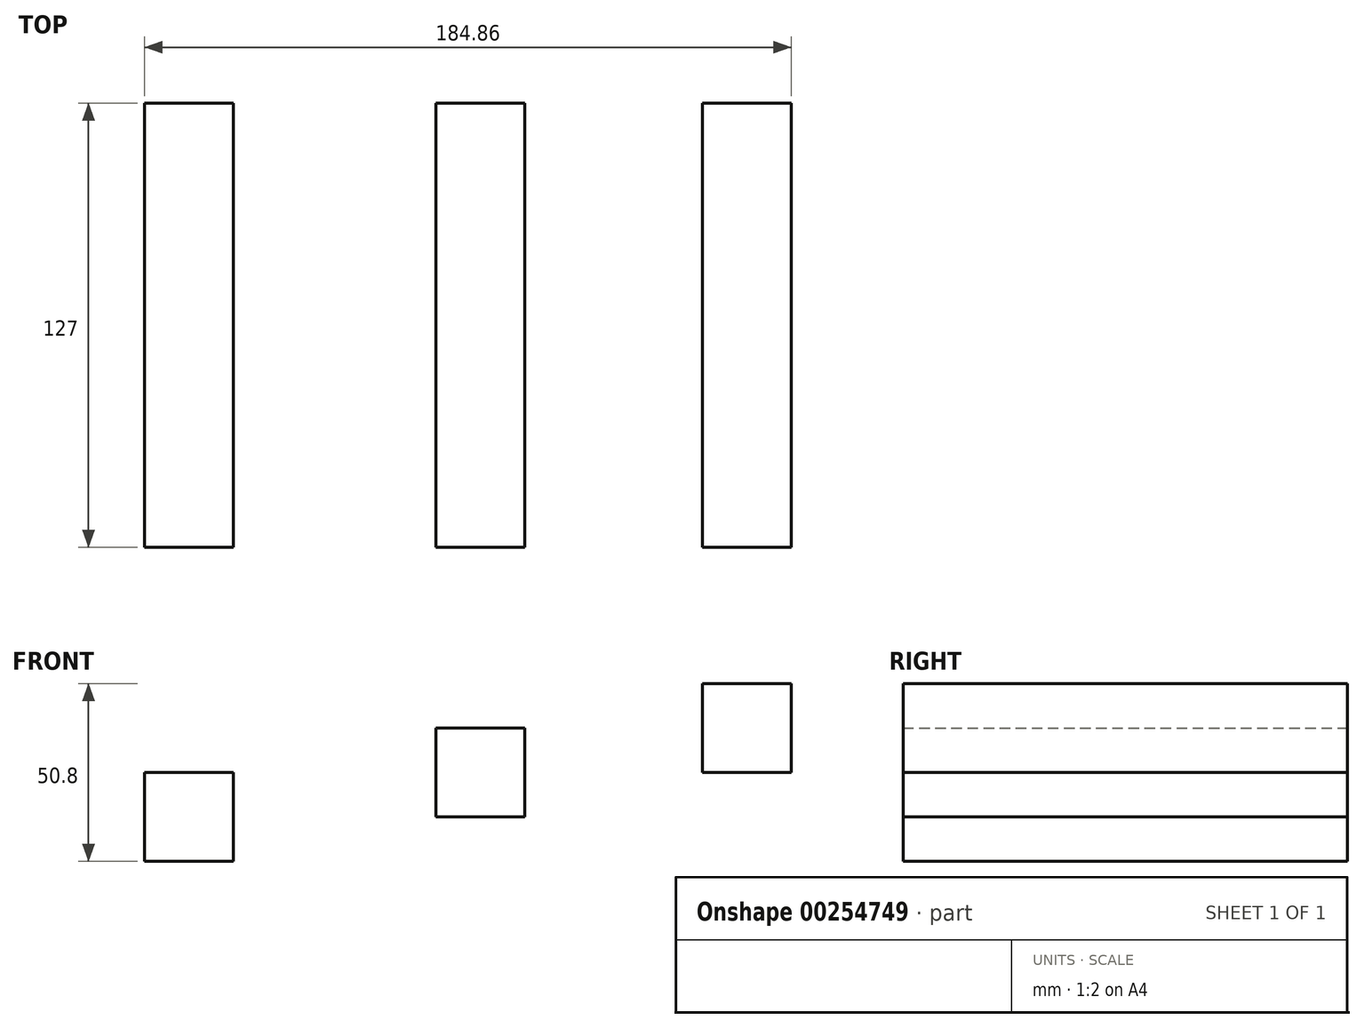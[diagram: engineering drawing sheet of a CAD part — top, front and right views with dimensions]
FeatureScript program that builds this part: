
annotation { "Feature Type Name" : "Feature", "Feature Type Description" : "" }
export const myFeature = defineFeature(function(context is Context, id is Id, definition is map)
    precondition{}
    {
        {
            var Q0;
            Q0=qCreatedBy(makeId("Front.planeOp"),FACE);
            var sketch = newSketch(context, id + "F0", { "sketchPlane" : qUnion([Q0])});
            skLineSegment(sketch, "E0.bottom", {"start": v(-68.29, 0) * mm, "end": v(-42.89, 0) * mm});
            skLineSegment(sketch, "E0.top", {"start": v(-68.29, 25.4) * mm, "end": v(-42.89, 25.4) * mm});
            skLineSegment(sketch, "E0.left", {"start": v(-68.29, 0) * mm, "end": v(-68.29, 25.4) * mm});
            skLineSegment(sketch, "E0.right", {"start": v(-42.89, 0) * mm, "end": v(-42.89, 25.4) * mm});
            skLineSegment(sketch, "E1", {"start": v(-39.36, 12.7) * mm, "end": v(11.44, 12.7) * mm});
            skPoint(sketch, "E1.startSnap0", {"position": v(-42.89, 12.7) * mm});
            skLineSegment(sketch, "E2.bottom", {"start": v(14.97, 12.7) * mm, "end": v(40.37, 12.7) * mm});
            skLineSegment(sketch, "E2.top", {"start": v(14.97, 38.1) * mm, "end": v(40.37, 38.1) * mm});
            skLineSegment(sketch, "E2.left", {"start": v(14.97, 12.7) * mm, "end": v(14.97, 38.1) * mm});
            skLineSegment(sketch, "E2.right", {"start": v(40.37, 12.7) * mm, "end": v(40.37, 38.1) * mm});
            skLineSegment(sketch, "E3", {"start": v(40.37, 25.4) * mm, "end": v(91.17, 25.4) * mm});
            skLineSegment(sketch, "E4.bottom", {"start": v(91.17, 25.4) * mm, "end": v(116.57, 25.4) * mm});
            skLineSegment(sketch, "E4.top", {"start": v(91.17, 50.8) * mm, "end": v(116.57, 50.8) * mm});
            skLineSegment(sketch, "E4.left", {"start": v(91.17, 25.4) * mm, "end": v(91.17, 50.8) * mm});
            skLineSegment(sketch, "E4.right", {"start": v(116.57, 25.4) * mm, "end": v(116.57, 50.8) * mm});
            skSolve(sketch);
        }
        {
            var Q0;
            Q0 = qSketchRegion(id + "F0", true);
            extrude(context, id + "F1", {"entities" : qUnion([Q0]), "depth" : 127 * mm});
        }
    });
